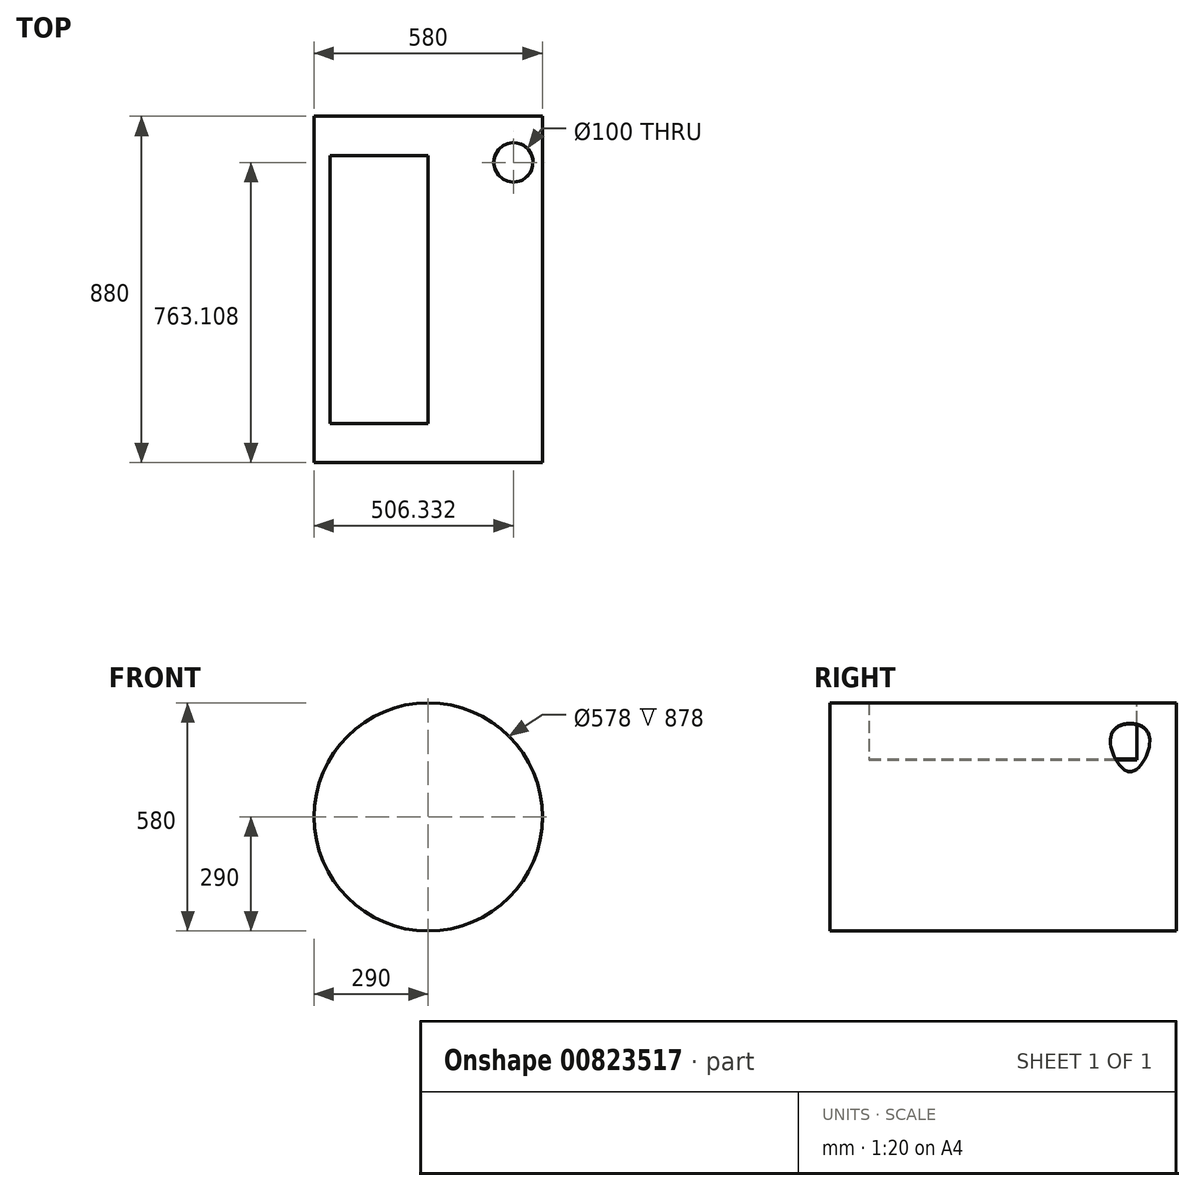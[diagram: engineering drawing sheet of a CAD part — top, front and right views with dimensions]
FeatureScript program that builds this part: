
annotation { "Feature Type Name" : "Feature", "Feature Type Description" : "" }
export const myFeature = defineFeature(function(context is Context, id is Id, definition is map)
    precondition{}
    {
        {
            var Q0;
            Q0=qCreatedBy(makeId("Front.planeOp"),FACE);
            var sketch = newSketch(context, id + "F0", { "sketchPlane" : qUnion([Q0])});
            skCircle(sketch, "E0", {"center": v(0, 0) * mm, "radius": 290 * mm});
            skSolve(sketch);
        }
        {
            var Q0;
            Q0 = qSketchRegion(id + "F0", true);
            extrude(context, id + "F1", {"entities" : qUnion([Q0]), "depth" : 880 * mm, "offsetDistance" : 25 * mm});
        }
        {
            var Q0;
            Q0=qCreatedBy(makeId("Top.planeOp"),FACE);
            var sketch = newSketch(context, id + "F2", { "sketchPlane" : qUnion([Q0])});
            skLineSegment(sketch, "E1", {"start": v(0, 0) * mm, "end": v(0, -100) * mm});
            skLineSegment(sketch, "E2", {"start": v(0, -100) * mm, "end": v(0, -880) * mm});
            skLineSegment(sketch, "E3", {"start": v(0, -880) * mm, "end": v(0, -780) * mm});
            skLineSegment(sketch, "E4", {"start": v(0, -780) * mm, "end": v(-250, -780) * mm});
            skLineSegment(sketch, "E5", {"start": v(-250, -780) * mm, "end": v(-250, -100) * mm});
            skLineSegment(sketch, "E6", {"start": v(-250, -100) * mm, "end": v(0, -100) * mm});
            skSolve(sketch);
        }
        {
            var Q0;
            Q0 = qSketchRegion(id + "F2", true);
            var Q1;
            Q1 = qConstructionFilter(qBodyType(qCreatedBy(id + "F2" ,EDGE), BodyType.WIRE), ConstructionObject.NO);
            extrude(context, id + "F3", {"entities" : qUnion([Q0]), "operationType" : NewBodyOperationType.REMOVE, "surfaceEntities" : qUnion([Q1]), "depth" : 566 * mm, "offsetDistance" : 25 * mm});
        }
        {
            var Q0;
            Q0=makeQuery(id+"F3.boolean.opBoolean","COPY",FACE,{"derivedFrom":makeQuery(id+"F3.opExtrude","SWEPT_FACE",FACE,{"disambiguationData":[OSD([sQuery(id+"F2.wireOp",EDGE,"E2")])]})});
            var Q1;
            Q1=makeQuery(id+"F3.boolean.opBoolean","COPY",FACE,{"derivedFrom":makeQuery(id+"F3.opExtrude","SWEPT_FACE",FACE,{"disambiguationData":[OSD([sQuery(id+"F2.wireOp",EDGE,"E5")])]})});
            var Q2;
            Q2=makeQuery(id+"F3.boolean.opBoolean","COPY",FACE,{"derivedFrom":makeQuery(id+"F3.opExtrude","CAP_FACE",FACE,{"disambiguationData":[OSD([sQuery(id+"F2.wireOp",EDGE,"E2"),sQuery(id+"F2.wireOp",EDGE,"E4"),sQuery(id+"F2.wireOp",EDGE,"E5"),sQuery(id+"F2.wireOp",EDGE,"E6")])],"isStart":true})});
            var Q3;
            Q3=makeQuery(id+"F3.boolean.opBoolean","COPY",FACE,{"derivedFrom":makeQuery(id+"F3.opExtrude","SWEPT_FACE",FACE,{"disambiguationData":[OSD([sQuery(id+"F2.wireOp",EDGE,"E4")])]})});
            var Q4;
            Q4=makeQuery(id+"F3.boolean.opBoolean","COPY",FACE,{"derivedFrom":makeQuery(id+"F3.opExtrude","SWEPT_FACE",FACE,{"disambiguationData":[OSD([sQuery(id+"F2.wireOp",EDGE,"E6")])]})});
            shell(context, id + "F4", {"entities" : qUnion([Q0, Q1, Q2, Q3, Q4]), "thickness" : 1 * mm});
        }
        {
            var Q0;
            Q0=qCreatedBy(makeId("Top.planeOp"),FACE);
            var sketch = newSketch(context, id + "F5", { "sketchPlane" : qUnion([Q0])});
            skCircle(sketch, "E7", {"center": v(216.33, -116.9) * mm, "radius": 50 * mm});
            skSolve(sketch);
        }
        {
            var Q0;
            Q0 = qSketchRegion(id + "F5", true);
            extrude(context, id + "F6", {"entities" : qUnion([Q0]), "operationType" : NewBodyOperationType.REMOVE, "depth" : 314 * mm, "offsetDistance" : 25 * mm});
        }
    });
